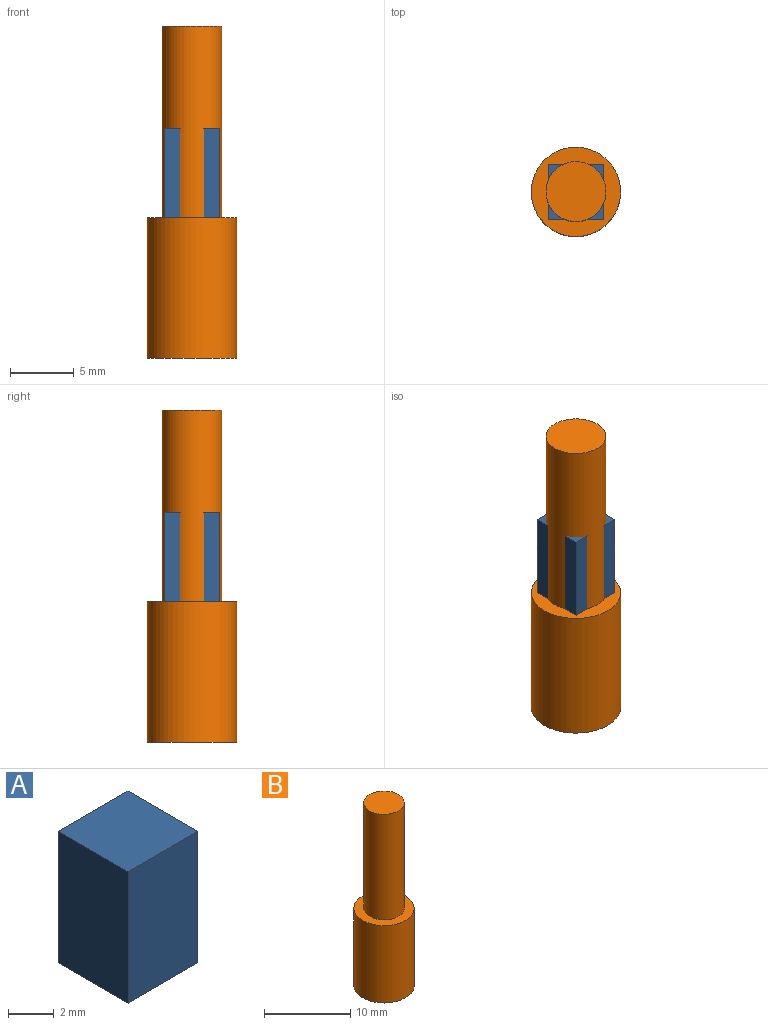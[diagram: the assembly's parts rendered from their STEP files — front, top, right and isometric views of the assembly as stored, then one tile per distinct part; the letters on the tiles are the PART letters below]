
ASSEMBLY  parts=2 mates=1
PART A: 6 faces, bbox 4.3x4.3x7 mm
  f0: plane 7x4.3mm, normal (0,-1,0), area 30.1mm2, adj f1,f3,f4,f5
  f1: plane 7x4.3mm, normal (1,0,0), area 30.1mm2, adj f0,f2,f4,f5
  f2: plane 7x4.3mm, normal (0,1,0), area 30.1mm2, adj f1,f3,f4,f5
  f3: plane 7x4.3mm, normal (-1,0,0), area 30.1mm2, adj f0,f2,f4,f5
  f4: plane 4.3x4.3mm, normal (0,0,1), area 18.5mm2, adj f0,f1,f2,f3
  f5: plane 4.3x4.3mm, normal (0,0,-1), area 18.5mm2, adj f0,f1,f2,f3
PART B: 5 faces, bbox 7x7x26 mm
  f0: cylinder r=3.5mm len=11mm, axis (0,0,-1), area 241.9mm2, adj f1,f2
  f1: plane 7x7mm, normal (0,0,1), area 21.1mm2, adj f0,f3
  f2: plane 7x7mm, normal (0,0,-1), area 38.5mm2, adj f0
  f3: cylinder r=2.35mm len=15mm, axis (0,0,-1), area 221.5mm2, adj f1,f4
  f4: plane 4.7x4.7mm, normal (0,0,1), area 17.3mm2, adj f3
PLACE A rot(axis=(0.71,0.71,0),180deg) t=(-4,4.59,0.85)mm
PLACE B t=(-4,4.59,-17.15)mm
MATE fastened A.f4 <-> B.f0  axis (0,0,-1) through (-4,4.59,-6.15)mm
